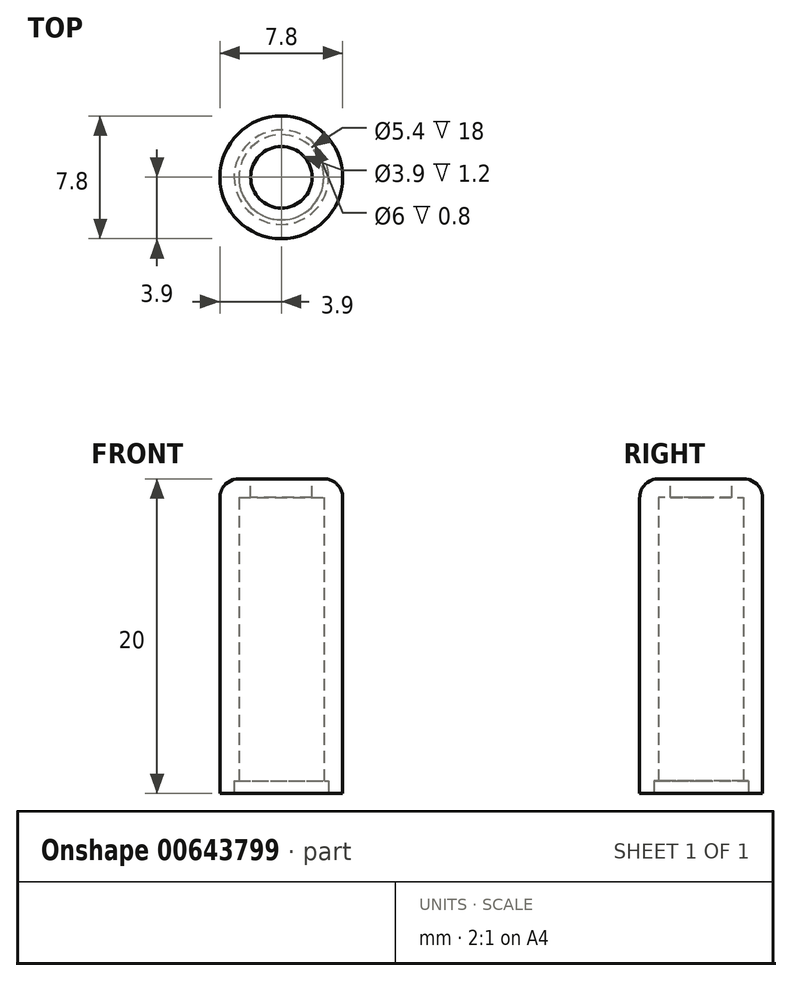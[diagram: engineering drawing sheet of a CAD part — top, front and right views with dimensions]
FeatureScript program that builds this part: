
annotation { "Feature Type Name" : "Feature", "Feature Type Description" : "" }
export const myFeature = defineFeature(function(context is Context, id is Id, definition is map)
    precondition{}
    {
        {
            var Q0;
            Q0=qCreatedBy(makeId("Top.planeOp"),FACE);
            var sketch = newSketch(context, id + "F0", { "sketchPlane" : qUnion([Q0])});
            skCircle(sketch, "E0", {"center": v(0, 0) * mm, "radius": 2.7 * mm});
            skCircle(sketch, "E1", {"center": v(0, 0) * mm, "radius": 3.9 * mm});
            skSolve(sketch);
        }
        {
            var Q0;
            Q0 = qSketchRegion(id + "F0", true);
            extrude(context, id + "F1", {"entities" : qUnion([Q0]), "depth" : 20 * mm, "offsetDistance" : 25 * mm});
        }
        {
            var Q0;
            Q0=makeQuery(id+"F1.opExtrude","CAP_FACE",FACE,{"disambiguationData":[OSD([sQuery(id+"F0.wireOp",EDGE,"E0"),sQuery(id+"F0.wireOp",EDGE,"E1")])],"isStart":false});
            var sketch = newSketch(context, id + "F2", { "sketchPlane" : qUnion([Q0])});
            skCircle(sketch, "E2", {"center": v(0, 0) * mm, "radius": 1.95 * mm});
            skCircle(sketch, "E3", {"center": v(0, 0) * mm, "radius": 2.7 * mm});
            skSolve(sketch);
        }
        {
            var Q0;
            Q0 = qSketchRegion(id + "F2", true);
            extrude(context, id + "F3", {"entities" : qUnion([Q0]), "operationType" : NewBodyOperationType.ADD, "oppositeDirection" : true, "depth" : 1.2 * mm, "offsetDistance" : 25 * mm});
        }
        {
            var Q0;
            Q0=makeQuery(id+"F1.opExtrude","CAP_EDGE",EDGE,{"disambiguationData":[OSD([sQuery(id+"F0.wireOp",EDGE,"E1")])],"isStart":false});
            fillet(context, id + "F4", {"entities" : qUnion([Q0]), "radius" : 1.2 * mm, "tangentPropagation" : true, "allowEdgeOverflow" : false});
        }
        {
            var Q0;
            Q0=makeQuery(id+"F1.opExtrude","CAP_FACE",FACE,{"disambiguationData":[OSD([sQuery(id+"F0.wireOp",EDGE,"E0"),sQuery(id+"F0.wireOp",EDGE,"E1")])],"isStart":true});
            var sketch = newSketch(context, id + "F5", { "sketchPlane" : qUnion([Q0])});
            skCircle(sketch, "E4", {"center": v(0, 0) * mm, "radius": 3 * mm});
            skSolve(sketch);
        }
        {
            var Q0;
            Q0 = qSketchRegion(id + "F5", true);
            extrude(context, id + "F6", {"entities" : qUnion([Q0]), "operationType" : NewBodyOperationType.REMOVE, "oppositeDirection" : true, "depth" : .8 * mm, "offsetDistance" : 25 * mm});
        }
    });
